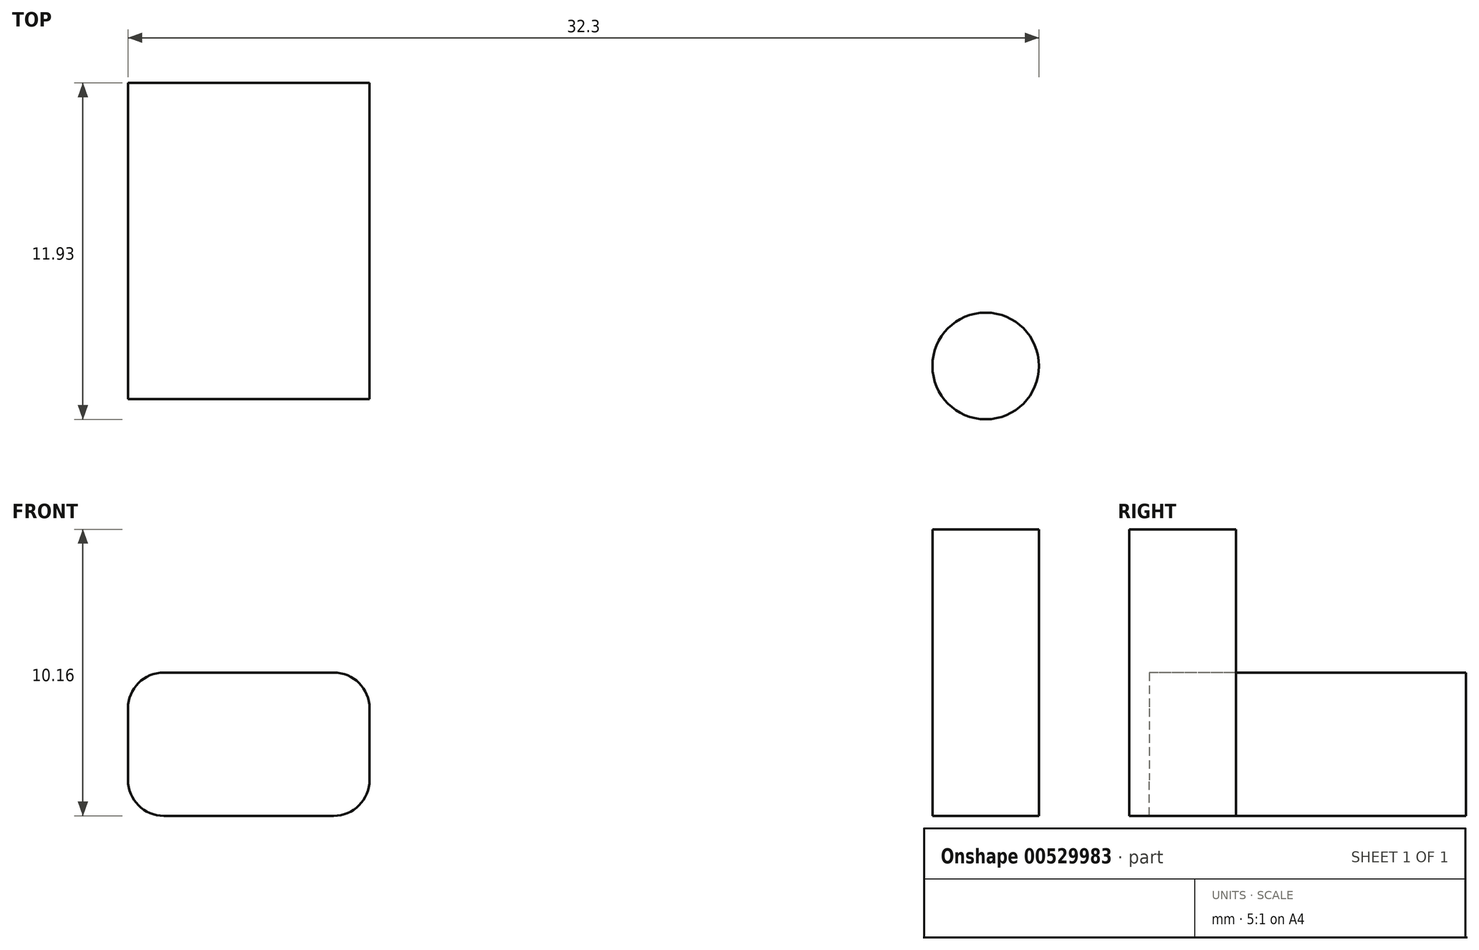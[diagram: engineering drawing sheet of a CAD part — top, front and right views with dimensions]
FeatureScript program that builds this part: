
annotation { "Feature Type Name" : "Feature", "Feature Type Description" : "" }
export const myFeature = defineFeature(function(context is Context, id is Id, definition is map)
    precondition{}
    {
        {
            var Q0;
            Q0=qCreatedBy(makeId("Top.planeOp"),FACE);
            var sketch = newSketch(context, id + "F0", { "sketchPlane" : qUnion([Q0])});
            skCircle(sketch, "E0", {"center": v(-31.6, 33.95) * mm, "radius": 1.9 * mm});
            skSolve(sketch);
        }
        {
            var Q0;
            Q0=makeQuery(id+"F0.imprint","IMPRINT",FACE,{"disambiguationData":[TD([[makeQuery(id+"F0.imprint","IMPRINT",EDGE,{"derivedFrom":sQuery(id+"F0.wireOp",EDGE,"E0")}),1.0]])]});
            extrude(context, id + "F1", {"entities" : qUnion([Q0]), "depth" : 10.16 * mm, "offsetDistance" : 25.4 * mm});
        }
        {
            var Q0;
            Q0=qCreatedBy(makeId("Top.planeOp"),FACE);
            var sketch = newSketch(context, id + "F2", { "sketchPlane" : qUnion([Q0])});
            skLineSegment(sketch, "E1.bottom", {"start": v(-62, 44) * mm, "end": v(-53.44, 44) * mm});
            skLineSegment(sketch, "E1.top", {"start": v(-62, 32.77) * mm, "end": v(-53.44, 32.77) * mm});
            skLineSegment(sketch, "E1.left", {"start": v(-62, 44) * mm, "end": v(-62, 32.77) * mm});
            skLineSegment(sketch, "E1.right", {"start": v(-53.44, 44) * mm, "end": v(-53.44, 32.77) * mm});
            skSolve(sketch);
        }
        {
            var Q0;
            Q0=makeQuery(id+"F2.imprint","IMPRINT",FACE,{"disambiguationData":[TD([[makeQuery(id+"F2.imprint","IMPRINT",EDGE,{"derivedFrom":sQuery(id+"F2.wireOp",EDGE,"E1.bottom")}),-1.0]])]});
            extrude(context, id + "F3", {"entities" : qUnion([Q0]), "depth" : 5.08 * mm, "offsetDistance" : 25.4 * mm});
        }
        {
            var Q0;
            Q0=makeQuery(id+"F3.opExtrude","CAP_EDGE",EDGE,{"disambiguationData":[OSD([sQuery(id+"F2.wireOp",EDGE,"E1.left")])],"isStart":false});
            fillet(context, id + "F4", {"entities" : qUnion([Q0]), "radius" : 1.27 * mm, "tangentPropagation" : true, "allowEdgeOverflow" : false});
        }
        {
            var Q0;
            Q0=makeQuery(id+"F3.opExtrude","CAP_EDGE",EDGE,{"disambiguationData":[OSD([sQuery(id+"F2.wireOp",EDGE,"E1.right")])],"isStart":false});
            fillet(context, id + "F5", {"entities" : qUnion([Q0]), "radius" : 1.27 * mm, "tangentPropagation" : true, "allowEdgeOverflow" : false});
        }
        {
            var Q0;
            Q0=makeQuery(id+"F3.opExtrude","CAP_EDGE",EDGE,{"disambiguationData":[OSD([sQuery(id+"F2.wireOp",EDGE,"E1.right")])],"isStart":true});
            fillet(context, id + "F6", {"entities" : qUnion([Q0]), "radius" : 1.27 * mm, "tangentPropagation" : true, "allowEdgeOverflow" : false});
        }
        {
            var Q0;
            Q0=makeQuery(id+"F3.opExtrude","CAP_EDGE",EDGE,{"disambiguationData":[OSD([sQuery(id+"F2.wireOp",EDGE,"E1.left")])],"isStart":true});
            fillet(context, id + "F7", {"entities" : qUnion([Q0]), "radius" : 1.27 * mm, "tangentPropagation" : true, "allowEdgeOverflow" : false});
        }
    });
